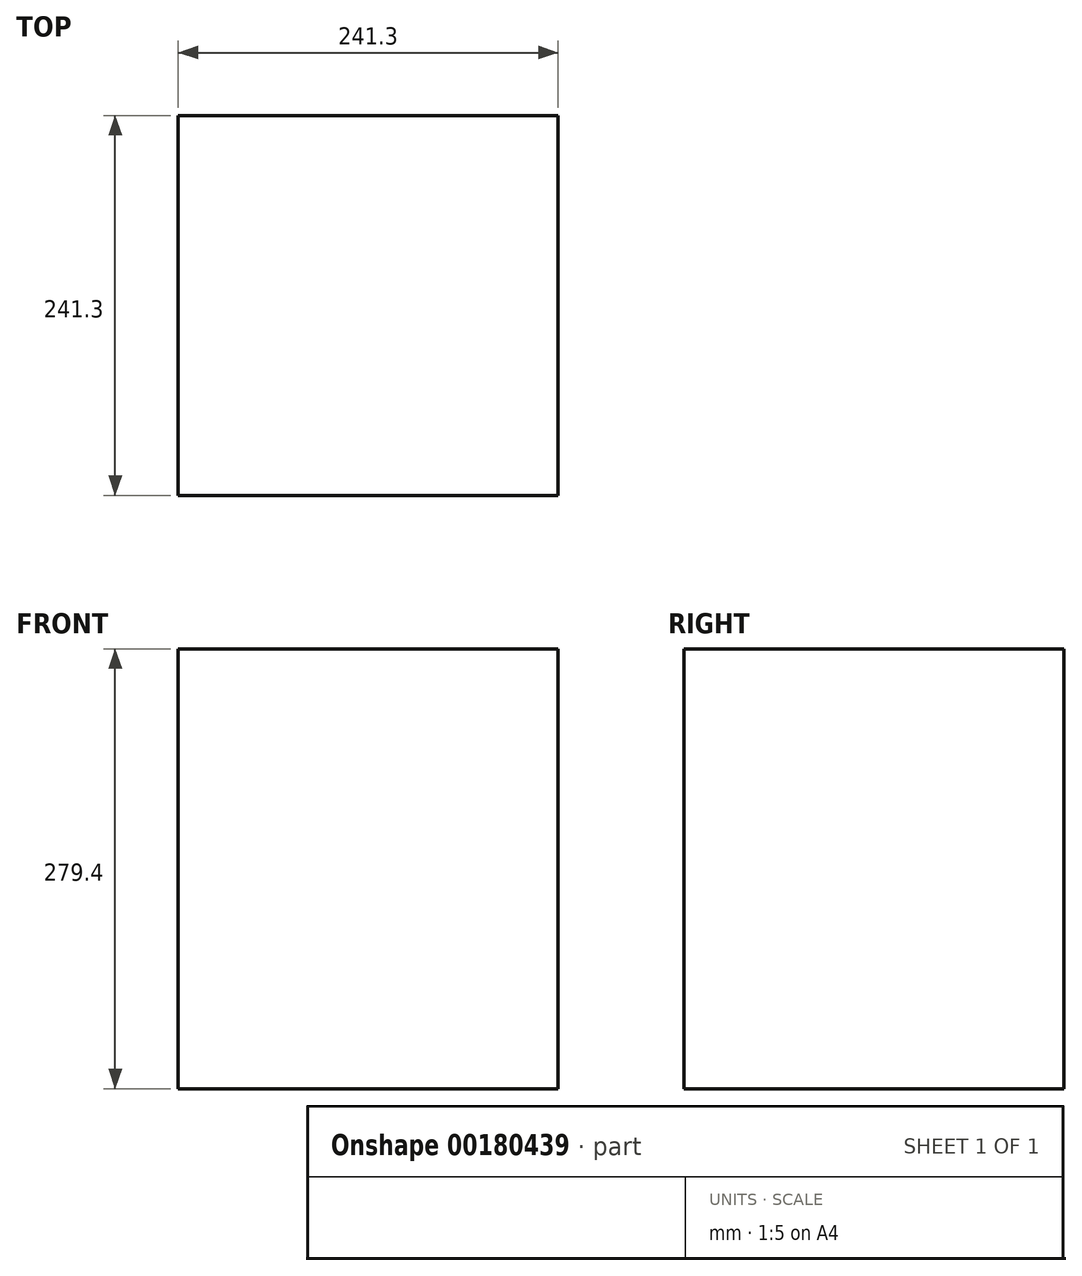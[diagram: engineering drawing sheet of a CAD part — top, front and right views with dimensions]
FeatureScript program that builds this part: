
annotation { "Feature Type Name" : "Feature", "Feature Type Description" : "" }
export const myFeature = defineFeature(function(context is Context, id is Id, definition is map)
    precondition{}
    {
        {
            var Q0;
            Q0=qCreatedBy(makeId("Top.planeOp"),FACE);
            var sketch = newSketch(context, id + "F0", { "sketchPlane" : qUnion([Q0])});
            skLineSegment(sketch, "E0.bottom", {"start": v(0, 0) * mm, "end": v(241.3, 0) * mm});
            skLineSegment(sketch, "E0.top", {"start": v(0, -241.3) * mm, "end": v(241.3, -241.3) * mm});
            skLineSegment(sketch, "E0.left", {"start": v(0, 0) * mm, "end": v(0, -241.3) * mm});
            skLineSegment(sketch, "E0.right", {"start": v(241.3, 0) * mm, "end": v(241.3, -241.3) * mm});
            skSolve(sketch);
        }
        {
            var Q0;
            Q0 = qSketchRegion(id + "F0", true);
            extrude(context, id + "F1", {"entities" : qUnion([Q0]), "depth" : 279.4 * mm});
        }
    });
